# Revit family: Trennsteg-OKA2 TW 60-AA
name_source: partatom
category: Generic Models
revit_build: Autodesk Revit 2017 (Build: 20160225_1515(x64)
units: mm (PartAtom-declared; Revit-internal decimal feet)

## family parameters
Always vertical = Yes
Can host rebar = No
Cut with Voids When Loaded = No
Part Type = Normal
Room Calculation Point = No
Round Connector Dimension = Use Diameter
Shared = No
Work Plane-Based = No

## types (11) — shared parameters
Length = 2400 mm
Manufacturer = Obo-Bettermann
Material = Strip-galvanised
URL = www.http://obo-bettermann.com

## per-type parameters (varying)
| type | GTIN | Height | Manufacturer Art.No. |
| OKA2 TW 30 | 4012195093893 | 30 mm  [stored 0.0984252 ft] | 7401984 |
| OKA2 TW 40 | 4012195093909 | 40 mm  [stored 0.131234 ft] | 7401988 |
| OKA2 TW 50 | 4012195093930 | 50 mm  [stored 0.164042 ft] | 7401992 |
| OKA2 TW 60 | 4012195093947 | 60 mm  [stored 0.19685 ft] | 7401996 |
| OKA2 TW 70 | 4012195093992 | 70 mm  [stored 0.229659 ft] | 7402000 |
| OKA2 TW 80 | 4012195094005 | 80 mm  [stored 0.262467 ft] | 7402004 |
| OKA2 TW 90 | 4012195094012 | 90 mm  [stored 0.295276 ft] | 7402008 |
| OKA2 TW 100 | 4012195093817 | 100 mm  [stored 0.328084 ft] | 7401960 |
| OKA2 TW 120 | 4012195093831 | 120 mm  [stored 0.393701 ft] | 7401968 |
| OKA2 TW 140 | 4012195093879 | 140 mm  [stored 0.459318 ft] | 7401976 |
| OKA2 TW 150 | 4012195093886 | 150 mm | 7401980 |

note: column(s) folded — value = type name in every type: Article Type

note: [stored X ft] marks values corroborated as IEEE doubles in the binary element streams (Revit-internal decimal feet)

## geometry (parser evidence)
native form markers: Sweep x3
no freeform markers — native parametric forms only
